# Revit family: Door_Crossing-Gard-Grille_BetweenJambMount_Cookson
name_source: partatom
category: Doors
revit_build: Autodesk Revit MEP 2013 (Build: 20130531_2115(x64)
units: mm (PartAtom-declared; Revit-internal decimal feet)

## types (12) — shared parameters
04 CSI = 08 33 00
95 CSI = 08330
Assembly Code = B2030410
Coil Dimension Note = 15” to 20” - Consult Cornell when dimensions are critical.
Cost Note = Based on size, materials selected. Consult Cookson.
Description = The security of a locked rolling grille that opens on alarm or power failure allowing safe escape.
Distributor Locator = http://www.cooksondoor.com
Drip Extension = 0' - 5"
From Coil Side Operate on Left = No
From Coil Side Operate on Right = Yes
Function = Interior
Height = 10' - 0"
Jamb Dimension Note = Between Jambs 5 1/2In to 6 1/2In wide. Consult Cookson when dimensions are critical.
LEED Information = http://www.cooksondoor.com
Listings = ICC-ES Evaluated for access controlled egress per the IBC®, per ESR-1167
Manufacturer = CornellCookson,Inc.
Model = ERG-IBC
Motor = Yes
Mounting = Between Jambs
Operator = Operator : Motor Operator
Operator Height = 5' - 4"
Optional aluminum, color anodized finish = No
Representative Disclaimer = Cookson products are sold and installed through a nationwide network of independent distributors.
Revit Object Download Link = http://cornellcookson.smartbim.com
Shutter Height = 9' - 7 51/256"
Shutter Width = 10' - 5 15/16"
Sizing Disclaimer = Openings from 5' to 24' wide and 4' to 20' high.
Subcategory = Roll Up
URL = www.cooksondoor.com/product/CrossingGard-Grilles
URL CAD = www.cooksondoor.com/architect-tools-and-resources/drawing-generator?prod=crossinggard
URL Photographs = www.cooksondoor.com/product/CrossingGard-Grilles
URL Specifications = http://www.cooksondoor.com
Wall Closure = By host
Wall Construction = Self supporting tubes, Masonry, Steel or Wood
Width = 10' - 0"

## per-type parameters (varying)
| type | Bottom Bar | Curtain Rods 2" OC Standard | Curtain Spacing Vertical Chains 3" OC | Curtain Spacing Vertical Chains 6" OC | Curtain Spacing Vertical Chains 9" OC | Guides | Hood |
| Motor Operated, Aluminium (Anodized Finish), 9" Vertical Spacing | Aluminum, mill finish(non-curtain components) | Aluminum, mill finish 3" Spacing (curtain only) | Yes | No | No | Aluminum, mill finish(non-curtain components) | Aluminum, mill finish(non-curtain components) |
| Motor Operated, Aluminium (Mill Finish), 9" Vertical Spacing | Aluminum, mill finish(non-curtain components) | Aluminum, mill finish 9" Spacing (curtain only) | No | No | Yes | Aluminum, mill finish(non-curtain components) | Aluminum, mill finish(non-curtain components) |
| Motor Operated, Galvanized Steel, 9" Vertical Spacing | Galvanized steel curtain, galvanized or powder coated plain steel components(non-curtain components) | Galvanized steel 9" Spacing (curtain only) | No | No | Yes | Galvanized steel curtain, galvanized or powder coated plain steel components(non-curtain components) | Galvanized steel curtain, galvanized or powder coated plain steel components(non-curtain components) |
| Motor Operated, Stainless Steel, 9" Vertical Spacing | Stainless steel(non-curtain components) | Stainless steel 9" Spacing (curtain only) | No | No | Yes | Stainless steel(non-curtain components) | Stainless steel(non-curtain components) |
| Motor Operated, Stainless Steel, 6" Vertical Spacing | Stainless steel(non-curtain components) | Stainless steel 6" Spacing (curtain only) | No | Yes | No | Stainless steel(non-curtain components) | Stainless steel(non-curtain components) |
| Motor Operated, Stainless Steel, 3" Vertical Spacing | Stainless steel(non-curtain components) | Stainless steel 3" Spacing (curtain only) | Yes | No | No | Stainless steel(non-curtain components) | Stainless steel(non-curtain components) |
| Motor Operated, Galvanized Steel, 6" Vertical Spacing | Galvanized steel curtain, galvanized or powder coated plain steel components(non-curtain components) | Galvanized steel 6" Spacing (curtain only) | No | Yes | No | Galvanized steel curtain, galvanized or powder coated plain steel components(non-curtain components) | Galvanized steel curtain, galvanized or powder coated plain steel components(non-curtain components) |
| Motor Operated, Galvanized Steel, 3" Vertical Spacing | Galvanized steel curtain, galvanized or powder coated plain steel components(non-curtain components) | Galvanized steel 3" Spacing (curtain only) | Yes | No | No | Galvanized steel curtain, galvanized or powder coated plain steel components(non-curtain components) | Galvanized steel curtain, galvanized or powder coated plain steel components(non-curtain components) |
| Motor Operated, Aluminium (Mill Finish), 6" Vertical Spacing | Aluminum, mill finish(non-curtain components) | Aluminum, mill finish 6" Spacing (curtain only) | No | Yes | No | Aluminum, mill finish(non-curtain components) | Aluminum, mill finish(non-curtain components) |
| Motor Operated, Aluminium (Mill Finish), 3" Vertical Spacing | Aluminum, mill finish(non-curtain components) | Aluminum, mill finish 3" Spacing (curtain only) | Yes | No | No | Aluminum, mill finish(non-curtain components) | Aluminum, mill finish(non-curtain components) |
| Motor Operated, Aluminium (Anodized Finish), 6" Vertical Spacing | Aluminum, anodized finish(non-curtain components) | Aluminum, anodized finish 6" Spacing (curtain only) | No | Yes | No | Aluminum, anodized finish(non-curtain components) | Aluminum, anodized finish(non-curtain components) |
| Motor Operated, Aluminium (Anodized Finish), 3" Vertical Spacing | Aluminum, anodized finish(non-curtain components) | Aluminum, anodized finish 3" Spacing (curtain only) | Yes | No | No | Aluminum, anodized finish(non-curtain components) | Aluminum, anodized finish(non-curtain components) |

## geometry (parser evidence)
native form markers: Blend x54, Sweep x13
no freeform markers — native parametric forms only
